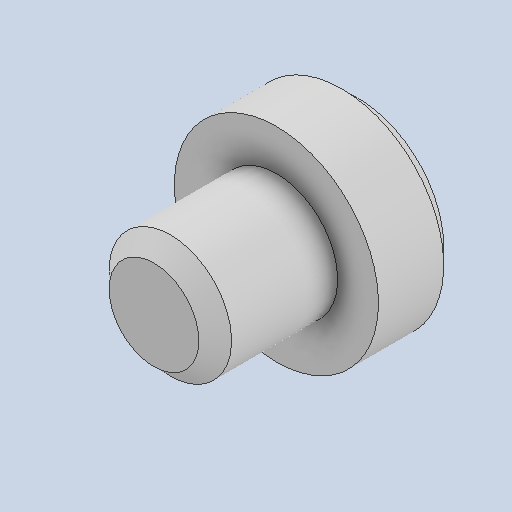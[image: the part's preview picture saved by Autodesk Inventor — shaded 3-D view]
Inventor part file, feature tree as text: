
AUTODESK INVENTOR PART (.ipt)
format: ipt  version: 2023 (Build 270158000, 158)  size: 115,200 bytes
history: native  units: mm
features: chamfer x1
ambient origin geometry x8: Origin, YZ Plane, XZ Plane, XY Plane, X Axis, Y Axis, Z Axis, Center Point
bodies: Solid1 (feature_tree)
feature tree (1):
  chamfer  "Chamfer2"  [1 undecoded]
note: 1 required parameter value undecoded (feature->parameter linkage not recoverable at this tier; creation-order binding heuristic only, values carry confidence <= 0.55)
